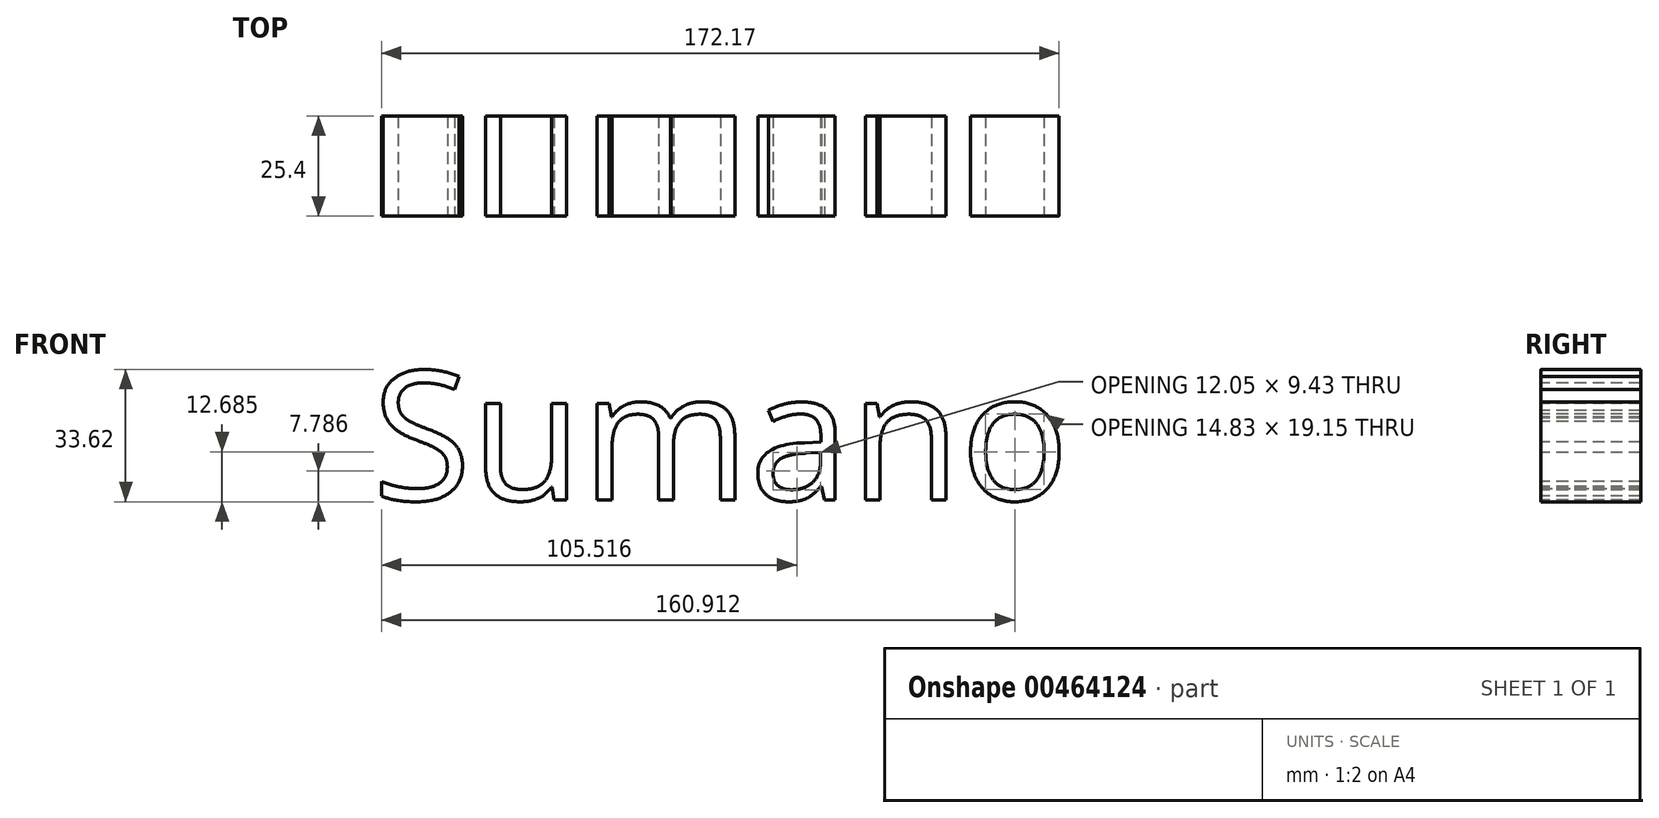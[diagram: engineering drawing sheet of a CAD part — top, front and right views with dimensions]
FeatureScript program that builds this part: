
annotation { "Feature Type Name" : "Feature", "Feature Type Description" : "" }
export const myFeature = defineFeature(function(context is Context, id is Id, definition is map)
    precondition{}
    {
        {
            var Q0;
            Q0=qCreatedBy(makeId("Front.planeOp"),FACE);
            var sketch = newSketch(context, id + "F0", { "sketchPlane" : qUnion([Q0])});
            skText(sketch, "E0", { "text": "Sumano", "fontName": "OpenSans-Regular.ttf"});
            const initialGuessF0  = {"E0": [-0.065, 0.0167, 1, 0, 0.03298]};
            skSetInitialGuess(sketch, initialGuessF0);
            skSolve(sketch);
        }
        {
            var Q0;
            Q0=makeQuery(id+"F0.imprint","IMPRINT",FACE,{"disambiguationData":[TD([[makeQuery(id+"F0.imprint","IMPRINT",EDGE,{"derivedFrom":sQuery(id+"F0.wireOp",EDGE,"E0.sketch_text.stroke-25")}),-1.0]])]});
            var Q1;
            Q1=makeQuery(id+"F0.imprint","IMPRINT",FACE,{"disambiguationData":[TD([[makeQuery(id+"F0.imprint","IMPRINT",EDGE,{"derivedFrom":sQuery(id+"F0.wireOp",EDGE,"E0.sketch_text.stroke-42")}),-1.0]])]});
            var Q2;
            Q2=makeQuery(id+"F0.imprint","IMPRINT",FACE,{"disambiguationData":[TD([[makeQuery(id+"F0.imprint","IMPRINT",EDGE,{"derivedFrom":sQuery(id+"F0.wireOp",EDGE,"E0.sketch_text.stroke-0")}),-1.0]])]});
            var Q3;
            Q3=makeQuery(id+"F0.imprint","IMPRINT",FACE,{"disambiguationData":[TD([[makeQuery(id+"F0.imprint","IMPRINT",EDGE,{"derivedFrom":sQuery(id+"F0.wireOp",EDGE,"E0.sketch_text.stroke-70")}),-1.0]])]});
            var Q4;
            Q4=makeQuery(id+"F0.imprint","IMPRINT",FACE,{"disambiguationData":[TD([[makeQuery(id+"F0.imprint","IMPRINT",EDGE,{"derivedFrom":sQuery(id+"F0.wireOp",EDGE,"E0.sketch_text.stroke-97")}),-1.0]])]});
            var Q5;
            Q5=makeQuery(id+"F0.imprint","IMPRINT",FACE,{"disambiguationData":[TD([[makeQuery(id+"F0.imprint","IMPRINT",EDGE,{"derivedFrom":sQuery(id+"F0.wireOp",EDGE,"E0.sketch_text.stroke-114")}),-1.0]])]});
            extrude(context, id + "F1", {"entities" : qUnion([Q0, Q1, Q2, Q3, Q4, Q5]), "oppositeDirection" : true, "depth" : 25.4 * mm});
        }
    });
